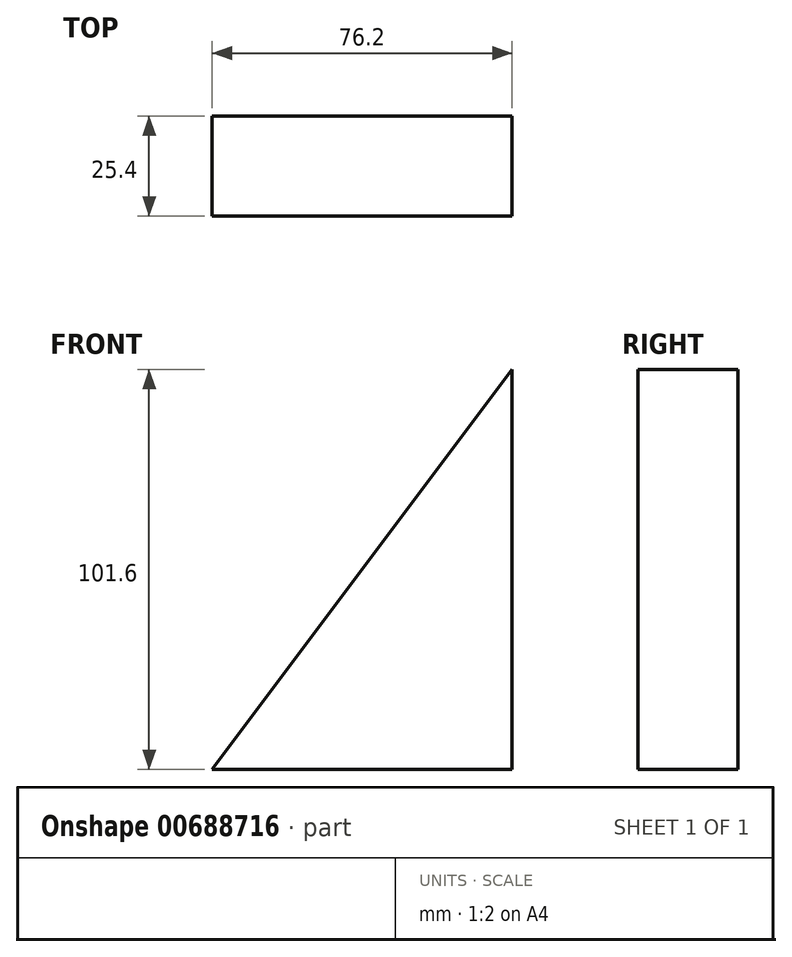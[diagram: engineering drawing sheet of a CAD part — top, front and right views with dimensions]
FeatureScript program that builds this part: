
annotation { "Feature Type Name" : "Feature", "Feature Type Description" : "" }
export const myFeature = defineFeature(function(context is Context, id is Id, definition is map)
    precondition{}
    {
        {
            var Q0;
            Q0=qCreatedBy(makeId("Front.planeOp"),FACE);
            var sketch = newSketch(context, id + "F0", { "sketchPlane" : qUnion([Q0])});
            skLineSegment(sketch, "E0.bottom", {"start": v(0, 0) * mm, "end": v(76.2, 0) * mm});
            skLineSegment(sketch, "E0.top", {"start": v(0, 50.8) * mm, "end": v(76.2, 50.8) * mm});
            skLineSegment(sketch, "E0.left", {"start": v(0, 0) * mm, "end": v(0, 50.8) * mm});
            skLineSegment(sketch, "E0.right", {"start": v(76.2, 0) * mm, "end": v(76.2, 50.8) * mm});
            skLineSegment(sketch, "E1.bottom", {"start": v(76.2, 50.8) * mm, "end": v(0, 50.8) * mm});
            skLineSegment(sketch, "E1.top", {"start": v(76.2, 101.6) * mm, "end": v(0, 101.6) * mm});
            skLineSegment(sketch, "E1.left", {"start": v(76.2, 50.8) * mm, "end": v(76.2, 101.6) * mm});
            skLineSegment(sketch, "E1.right", {"start": v(0, 50.8) * mm, "end": v(0, 101.6) * mm});
            skLineSegment(sketch, "E2", {"start": v(0, 101.6) * mm, "end": v(-76.2, 0) * mm});
            skLineSegment(sketch, "E3", {"start": v(-76.2, 0) * mm, "end": v(0, 0) * mm});
            skSolve(sketch);
        }
        {
            var Q0;
            Q0=makeQuery(id+"F0.imprint","IMPRINT",FACE,{"disambiguationData":[TD([[makeQuery(id+"F0.imprint","IMPRINT",EDGE,{"derivedFrom":sQuery(id+"F0.wireOp",EDGE,"E0.left")}),1.0]])]});
            extrude(context, id + "F1", {"entities" : qUnion([Q0]), "depth" : 25.4 * mm, "offsetDistance" : 25.4 * mm});
        }
    });
